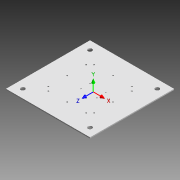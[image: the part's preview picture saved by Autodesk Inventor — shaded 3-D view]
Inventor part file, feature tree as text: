
AUTODESK INVENTOR PART (.ipt)
format: ipt  version: 2015 (Build 190159000, 159)  size: 247,808 bytes
history: native  units: in
note: dims shown in document units (in); Inventor stores cm internally (conversion verified against a paired STEP export)
features: reference x13, other x11, sketch x6, hole x2, sheet_metal_op x1
ambient origin geometry x8: Origin, YZ Plane, XZ Plane, XY Plane, X Axis, Y Axis, Z Axis, Center Point
bodies: Solid1 (feature_tree)
feature tree (33):
  sheet_metal_op  "Face1"
  other  "UCS1"
  hole  "Hole1"  [1 undecoded]
  hole  "Hole2"  [1 undecoded]
  sketch  "Sketch9"  dims[d39=0.125in]
  sketch  "Sketch1"  dims[d1=0.7874in d3=0.7874in d5=0.7874in d7=0.7874in d9=0.7874in d11=0.7874in d13=0.7874in d15=0.7874in d16=0.75in d17=0.75in d18=0.75in d19=0.75in d20=0.25in d21=0.25in d22=0.25in d23=0.25in d24=2.5681in d25=0.375in d26=1.5in d27=1.5in d28=1.5in d29=1.5in d30=1.5in d31=1.5in d32=1.5in d33=1.5in d34=90.0deg]
  other  "Plate1"
  sketch  "Sketch2"  dims[d35=45.0deg d36=90.0deg]
  sketch  "Sketch7"  dims[d37=90.0deg]
  sketch  "Sketch8"  dims[d38=90.0deg]
  sketch  "Sketch10"  dims[d40=0.75in d41=0.75in d42=5.313in d43=6.063in d44=11.376in d45=6.063in d46=0.25in d47=0.0in d48=4.2872in d49=5.9746in d50=6.063in d51=0.25in d52=8.3244in d53=4.2872in d54=0.125in d55=8.4494in d56=0.0625in d57=10.0in d58=10.0in d59=0.125in d60=8.0in d61=0.5in d62=0.5in d63=0.5in d64=0.5in d65=0.125in d66=0.0in d70=-2.5491in d71=0.0in d72=3.032in d73=0.0in d74=0.0in d75=0.0in d76=0.14in d77=0.75in d78=0.375in d79=0.25in d80=0.5635in d81=0.125in d82=0.8108in d83=0.144in d84=0.75in d85=0.279in d86=0.25in d87=0.5635in d88=0.125in d89=0.8108in d90=3.6662in d91=4.4695in d92=0.125in d93=0.0in]
  reference  "Reference1"
  reference  "Reference2"
  reference  "Reference3"
  reference  "Reference4"
  reference  "Reference5"
  reference  "Reference6"
  reference  "Reference7"
  reference  "Reference8"
  reference  "Reference9"
  reference  "Reference10"
  reference  "Reference11"
  reference  "Reference12"
  reference  "Reference13"
  other  "Cut1"
  other  "Cut2"
  other  "UCS1: YZ Plane"
  other  "UCS1: XZ Plane"
  other  "UCS1: XY Plane"
  other  "UCS1: X Axis"
  other  "UCS1: Y Axis"
  other  "UCS1: Z Axis"
  other  "UCS1: Center Point"
note: 2 required parameter values undecoded (feature->parameter linkage not recoverable at this tier; creation-order binding heuristic only, values carry confidence <= 0.55)
